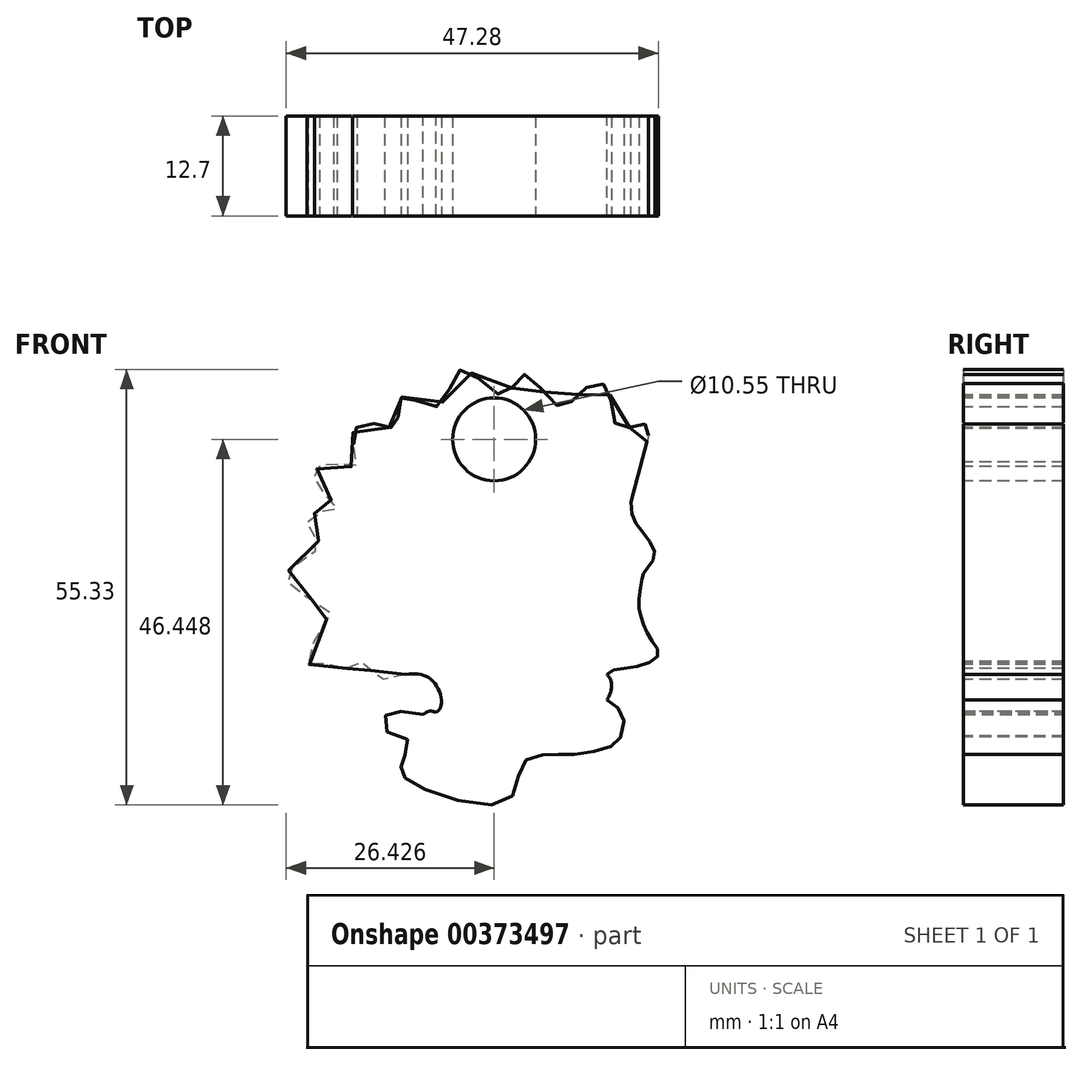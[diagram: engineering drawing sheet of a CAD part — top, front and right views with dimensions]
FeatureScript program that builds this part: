
annotation { "Feature Type Name" : "Feature", "Feature Type Description" : "" }
export const myFeature = defineFeature(function(context is Context, id is Id, definition is map)
    precondition{}
    {
        {
            var Q0;
            Q0=qCreatedBy(makeId("Front.planeOp"),FACE);
            var sketch = newSketch(context, id + "F0", { "sketchPlane" : qUnion([Q0])});
            skFitSpline(sketch, "E0", {"points": [v(-30.63, 9.45) * mm, v(-32.46, 8.64) * mm, v(-36.72, 9.25) * mm, v(-37.94, 9.25) * mm, v(-35.3, 15.13) * mm, v(-34.69, 15.33) * mm, v(-38.95, 18.17) * mm, v(-40.57, 20.8) * mm, v(-36.52, 24.26) * mm, v(-37.94, 26.29) * mm, v(-37.12, 28.31) * mm, v(-34.28, 28.92) * mm, v(-36.72, 31.76) * mm, v(-36.92, 33.8) * mm, v(-35.3, 34.8) * mm, v(-31.85, 34.4) * mm, v(-32.26, 38.46) * mm, v(-29.42, 39.67) * mm, v(-26.78, 39.47) * mm, v(-25.97, 43.12) * mm, v(-21.5, 41.9) * mm, v(-18.46, 46.57) * mm, v(-13.19, 43.33) * mm, v(-10.55, 45.96) * mm, v(-6.09, 41.9) * mm, v(-3.04, 43.94) * mm, v(0, 44.34) * mm, v(1.42, 39.27) * mm, v(4.67, 39.67) * mm, v(5.27, 38.25) * mm, v(3.04, 29.73) * mm, v(4.26, 26.29) * mm, v(6.09, 23.04) * mm, v(4.87, 21.01) * mm, v(4.46, 20) * mm, v(4.06, 16.95) * mm, v(4.46, 14.72) * mm, v(5.48, 12.5) * mm, v(6.5, 10.26) * mm, v(2.64, 8.64) * mm, v(0, 7.83) * mm, v(0, 4.58) * mm, v(1.83, 3.16) * mm, v(1.83, 0) * mm, v(0, -1.5) * mm, v(-4.46, -2.32) * mm, v(-7.5, -2.32) * mm, v(-10.75, -3.53) * mm, v(-12.58, -8.2) * mm, v(-24.34, -6.17) * mm, v(-26.17, -4.14) * mm, v(-25.56, -2.11) * mm, v(-25.56, 0) * mm, v(-27.39, 0) * mm, v(-28, 2.75) * mm, v(-23.33, 2.75) * mm, v(-21.1, 3.77) * mm, v(-22.11, 7.01) * mm, v(-25.56, 7.83) * mm, v(-29.42, 7.42) * mm, v(-30.63, 9.45) * mm]});
            skFitSpline(sketch, "E1", {"points": [v(-25.56, 7.83) * mm, v(-22.11, 9.65) * mm, v(-17.85, 9.45) * mm, v(-11.97, 7.83) * mm, v(-5.48, 7.83) * mm, v(0, 7.83) * mm, v(0, 4.58) * mm, v(-1.83, 2.55) * mm, v(0, 3.16) * mm, v(-2.84, 0) * mm, v(-7.3, 0) * mm, v(-11.97, 0) * mm, v(-16.23, 0) * mm, v(-22.11, 3.16) * mm, v(-23.33, 2.75) * mm], "startDerivative": vector(47.7, 32.51) * mm, "endDerivative": vector(-24.33, -19.44) * mm});
            skFitSpline(sketch, "E2", {"points": [v(-28, 14.52) * mm, v(-28, 19.8) * mm, v(-25.36, 21.21) * mm, v(-22.11, 21.82) * mm, v(-22.11, 23.24) * mm, v(-22.11, 28.11) * mm, v(3.04, 29.73) * mm], "startDerivative": vector(-5.68, 38.35) * mm, "endDerivative": vector(96.96, -6.67) * mm});
            skFitSpline(sketch, "E3", {"points": [v(-18.66, 21.42) * mm, v(-19.68, 18.78) * mm, v(-18.66, 16.14) * mm, v(-17.45, 14.72) * mm, v(-15.01, 13.91) * mm, v(-13.19, 14.93) * mm, v(-11.56, 16.55) * mm, v(-11.36, 18.58) * mm, v(-11.16, 20.6) * mm], "startDerivative": vector(-11.18, -18.6) * mm, "endDerivative": vector(2.5, 16.98) * mm});
            skFitSpline(sketch, "E4", {"points": [v(-19.07, 18.58) * mm, v(-12.17, 18.58) * mm], "startDerivative": vector(6.9, 0) * mm, "endDerivative": vector(6.9, 0) * mm});
            skFitSpline(sketch, "E5", {"points": [v(-3.65, 18.37) * mm, v(-1.62, 15.53) * mm, v(1.83, 14.93) * mm, v(3.45, 17.36) * mm, v(3.45, 20) * mm, v(3.25, 21.62) * mm], "startDerivative": vector(6.97, -14.33) * mm, "endDerivative": vector(-1.3, 9.98) * mm});
            skFitSpline(sketch, "E6", {"points": [v(3.04, 19.19) * mm, v(-3.65, 18.98) * mm], "startDerivative": vector(-6.7, -0.2) * mm, "endDerivative": vector(-6.7, -0.2) * mm});
            skFitSpline(sketch, "E7", {"points": [v(-6.09, 20) * mm, v(-5.68, 17.56) * mm, v(-4.87, 15.94) * mm, v(-2.03, 14.32) * mm, v(0.81, 12.5) * mm, v(-0.6, 10.67) * mm, v(-3.04, 10.26) * mm, v(-6.09, 10.26) * mm, v(-7.91, 10.87) * mm, v(-8.72, 12.7) * mm, v(-7.7, 14.11) * mm], "startDerivative": vector(3.3, -25.27) * mm, "endDerivative": vector(16.65, 15) * mm});
            skFitSpline(sketch, "E8", {"points": [v(-17.85, 9.45) * mm, v(-17.85, 0.78) * mm], "startDerivative": vector(0, -8.67) * mm, "endDerivative": vector(0, -8.67) * mm});
            skFitSpline(sketch, "E9", {"points": [v(-12.98, 7.62) * mm, v(-13.8, -0.5) * mm], "startDerivative": vector(-0.81, -8.11) * mm, "endDerivative": vector(-0.81, -8.11) * mm});
            skFitSpline(sketch, "E10", {"points": [v(-7.5, 7.01) * mm, v(-7.5, 0.52) * mm], "startDerivative": vector(0, -6.5) * mm, "endDerivative": vector(0, -6.5) * mm});
            skFitSpline(sketch, "E11", {"points": [v(-2.43, 7.22) * mm, v(-2.84, 0.93) * mm], "startDerivative": vector(-0.4, -6.29) * mm, "endDerivative": vector(-0.4, -6.29) * mm});
            skSolve(sketch);
        }
        {
            var Q0;
            Q0 = qSketchRegion(id + "F0", true);
            extrude(context, id + "F1", {"entities" : qUnion([Q0]), "depth" : 12.7 * mm, "offsetDistance" : 25.4 * mm});
        }
        {
            var Q0;
            Q0=makeQuery(id+"F1.opExtrude","CAP_FACE",FACE,{"disambiguationData":[OSD([sQuery(id+"F0.wireOp",EDGE,"E0"),sQuery(id+"F0.wireOp",EDGE,"E1")])],"isStart":false});
            var sketch = newSketch(context, id + "F2", { "sketchPlane" : qUnion([Q0])});
            skCircle(sketch, "E12", {"center": v(-14.31, 37.7) * mm, "radius": 5.28 * mm});
            skSolve(sketch);
        }
        {
            var Q0;
            Q0=makeQuery(id+"F2.imprint","IMPRINT",FACE,{"disambiguationData":[TD([[makeQuery(id+"F2.imprint","IMPRINT",EDGE,{"derivedFrom":sQuery(id+"F2.wireOp",EDGE,"E12")}),1.0]])]});
            extrude(context, id + "F3", {"entities" : qUnion([Q0]), "operationType" : NewBodyOperationType.REMOVE, "oppositeDirection" : true, "depth" : 25.4 * mm, "offsetDistance" : 25.4 * mm});
        }
    });
